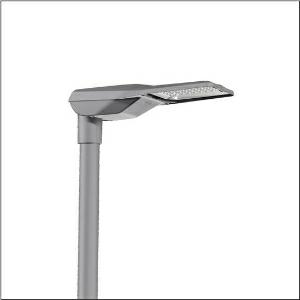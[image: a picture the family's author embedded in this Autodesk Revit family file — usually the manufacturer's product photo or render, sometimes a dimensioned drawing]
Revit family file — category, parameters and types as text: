
# Revit family: streetlight_sl_21_iq_mini___p0_5a_5xe2v31g08hb_63cb
name_source: partatom
category: Lighting Fixtures
units: mm (PartAtom-declared; Revit-internal decimal feet)

## family parameters
Cut with Voids When Loaded = No
Host = Face
Light Source = No
Part Type = Normal
Room Calculation Point = No
Round Connector Dimension = Use Diameter
Shared = No

## types (1)
- --- (1 x LED, 9290 lm, 70.9 W, 3000K)
    Apparent Load = 71 VA
    CIE Flux Codes = 37 73 96 100 100
    Color Rendering = 70
    Color Temperature = 3000K
    Default Elevation = 1800 mm
    Description = Streetlight SL 21 iQ mini, mast luminaire, primary light control with lens, of PMMA, primary optical cover: cover, of toughened safety glass, transparent, light distribution: P0.5a, light emission: direct distribution, primary light characteristic: asymmetric, installation type: post-top, side-entry, LED, High Power LED, rated luminous flux: 9.290lm, luminous efficacy: 131lm/W, light colour: 730, colour temperature: 3000K, control gear: iQ Street-Remote, control: pre-setting: linear dimming characteristic, Street-Remote, Auto-Match, Temp-Guard, Lumen-Switch, Night-Set, Smart-Wire, Light-Fading, Desk-Remote (wireless, voltage-free reading and setting of iQ features in the workshop via application-optimized NFC function/RFID function), optimised constant luminous flux control (CLO 2.0), mains connection: 220..240V, AC, 50/60Hz, start of lifetime: 71W, end of service life: 75W, reduction: 31W, luminaire housing, of diecast aluminium, powder-coated, Siteco® metallic grey (DB 702S), corrosivity category C5 mid according to DIN EN ISO 12944, please order mast flange separately, inclination adjustable: 0°, 5°, 10°, 15°, sealing non-destructively replaceable, multi-level sealing system, length: 628mm, width: 235mm, height: 110mm, mast flange for spigot size: 42mm (side-entry): 5XC10008XM4, 60/48mm (side-entry/post-top): 5XC10108XM2, 76/60mm (side-entry/post-top): 5XC10108XM1, mounting height: 4..8m, protection rating (complete): IP66, insulation class (complete): insulation class II (safety insulation), certification: CE, ENEC, ENEC+, VDE, impact resistance: IK10, permissible operating ambient temperature for outdoor applications: -40..+50°C, standard-compliant lighting for roads and squares, packaging unit: 1 piece

Light Distribution: P0.5a
    Height = 110 mm
    Lamp = 1 x LED
    Lamp Light Flux = 9290 lm
    Lamp Power = 70.9 W
    Lamp count = 1
    Length = 625 mm
    Luminous efficacy = 131 lm/W
    Manufacturer = Siteco
    ModVariant = No
    Model = 5XE2V31G08HB
    Number of Poles = 1
    OnlyDefault = Yes
    Power Factor = 1
    Product Name = Streetlight SL 21 iQ mini | P0.5a
    Product group = mast luminaire | pylon top
    ProductGroupID = 6100
    Protection Class = Protection class II
    Protection Degree = IP 66
    RLX_Detail_Level = 1
    RLX_Emergency_Light_Flux = 0 lm
    RLX_Emergency_Type = 0
    RLX_Emergency_Type_DB = No
    RlxData = <blob elided: 25917 chars, md5=85b0e349>
    Socket = socket
    Standby Power = 0 W
    System Light Flux = 9290 lm
    System Power = 71 W
    Type Comments = factory setting: luminous flux: 100 % | dim-lin: 254 | 711 mA
    Type Image = l_1003519.jpg
    URL = http://relux.com
    VarID = @adj_069692
    Voltage = 0 V
    Weight = 0.00 kg
    Width = 234 mm

## geometry (parser evidence)
native form markers: Blend x4, Sweep x12
no freeform markers — native parametric forms only
